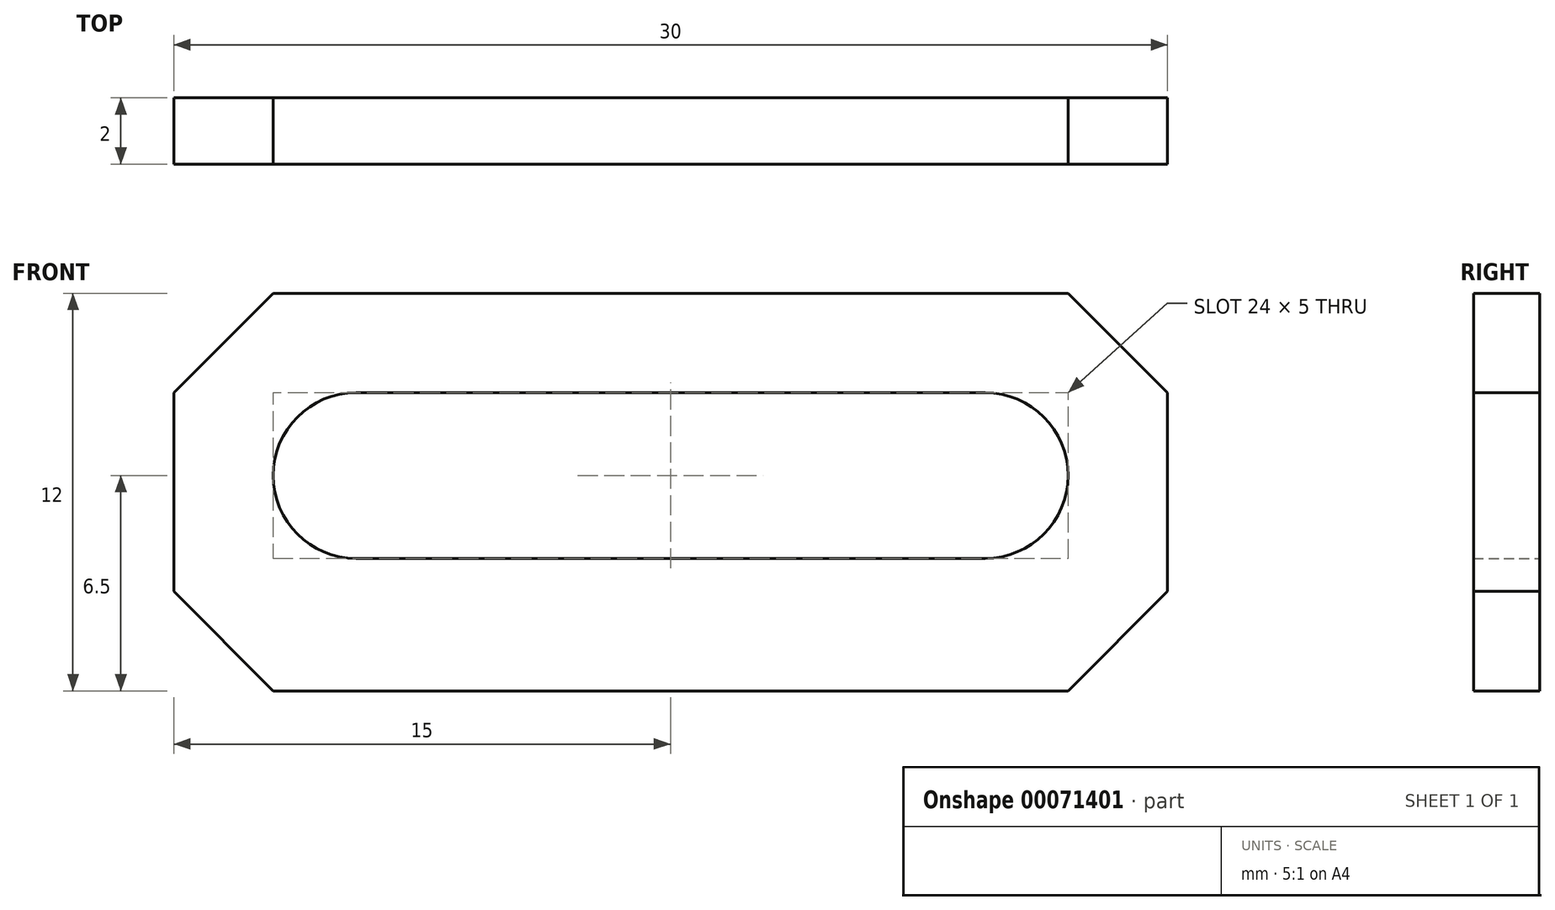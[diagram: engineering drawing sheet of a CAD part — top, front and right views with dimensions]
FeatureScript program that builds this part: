
annotation { "Feature Type Name" : "Feature", "Feature Type Description" : "" }
export const myFeature = defineFeature(function(context is Context, id is Id, definition is map)
    precondition{}
    {
        {
            var Q0;
            Q0=qCreatedBy(makeId("Front.planeOp"),FACE);
            var sketch = newSketch(context, id + "F0", { "sketchPlane" : qUnion([Q0])});
            skLineSegment(sketch, "E0", {"start": v(0, 0) * mm, "end": v(30, 0) * mm});
            skLineSegment(sketch, "E1", {"start": v(30, 0) * mm, "end": v(30, -12) * mm});
            skLineSegment(sketch, "E2", {"start": v(30, -12) * mm, "end": v(0, -12) * mm});
            skLineSegment(sketch, "E3", {"start": v(0, -12) * mm, "end": v(0, 0) * mm});
            skPoint(sketch, "E4.positionSnap0", {"position": v(15, -6) * mm});
            skArc(sketch, "E5.0.startCap", {"start": v(5.5, -8) * mm, "mid": v(3, -5.5) * mm, "end": v(5.5, -3) * mm});
            skArc(sketch, "E5.0.endCap", {"start": v(24.5, -3) * mm, "mid": v(27, -5.5) * mm, "end": v(24.5, -8) * mm});
            skLineSegment(sketch, "E5.0.left", {"start": v(5.5, -3) * mm, "end": v(24.5, -3) * mm});
            skLineSegment(sketch, "E5.0.right", {"start": v(5.5, -8) * mm, "end": v(24.5, -8) * mm});
            skSolve(sketch);
        }
        {
            var Q0;
            Q0=makeQuery(id+"F0.imprint","IMPRINT",FACE,{"disambiguationData":[TD([[makeQuery(id+"F0.imprint","IMPRINT",EDGE,{"derivedFrom":sQuery(id+"F0.wireOp",EDGE,"E0")}),-1.0]])]});
            extrude(context, id + "F1", {"entities" : qUnion([Q0]), "depth" : 2 * mm});
        }
        {
            var Q0;
            Q0=makeQuery(id+"F1.opExtrude","SWEPT_EDGE",EDGE,{"disambiguationData":[OSD([sQuery(id+"F0.wireOp",EDGE,"E0"),sQuery(id+"F0.wireOp",EDGE,"E3")])]});
            var Q1;
            Q1=makeQuery(id+"F1.opExtrude","SWEPT_EDGE",EDGE,{"disambiguationData":[OSD([sQuery(id+"F0.wireOp",EDGE,"E0"),sQuery(id+"F0.wireOp",EDGE,"E1")])]});
            var Q2;
            Q2=makeQuery(id+"F1.opExtrude","SWEPT_EDGE",EDGE,{"disambiguationData":[OSD([sQuery(id+"F0.wireOp",EDGE,"E2"),sQuery(id+"F0.wireOp",EDGE,"E3")])]});
            var Q3;
            Q3=makeQuery(id+"F1.opExtrude","SWEPT_EDGE",EDGE,{"disambiguationData":[OSD([sQuery(id+"F0.wireOp",EDGE,"E1"),sQuery(id+"F0.wireOp",EDGE,"E2")])]});
            chamfer(context, id + "F2", {"entities" : qUnion([Q0, Q1, Q2, Q3]), "width" : 3 * mm, "tangentPropagation" : true});
        }
    });
